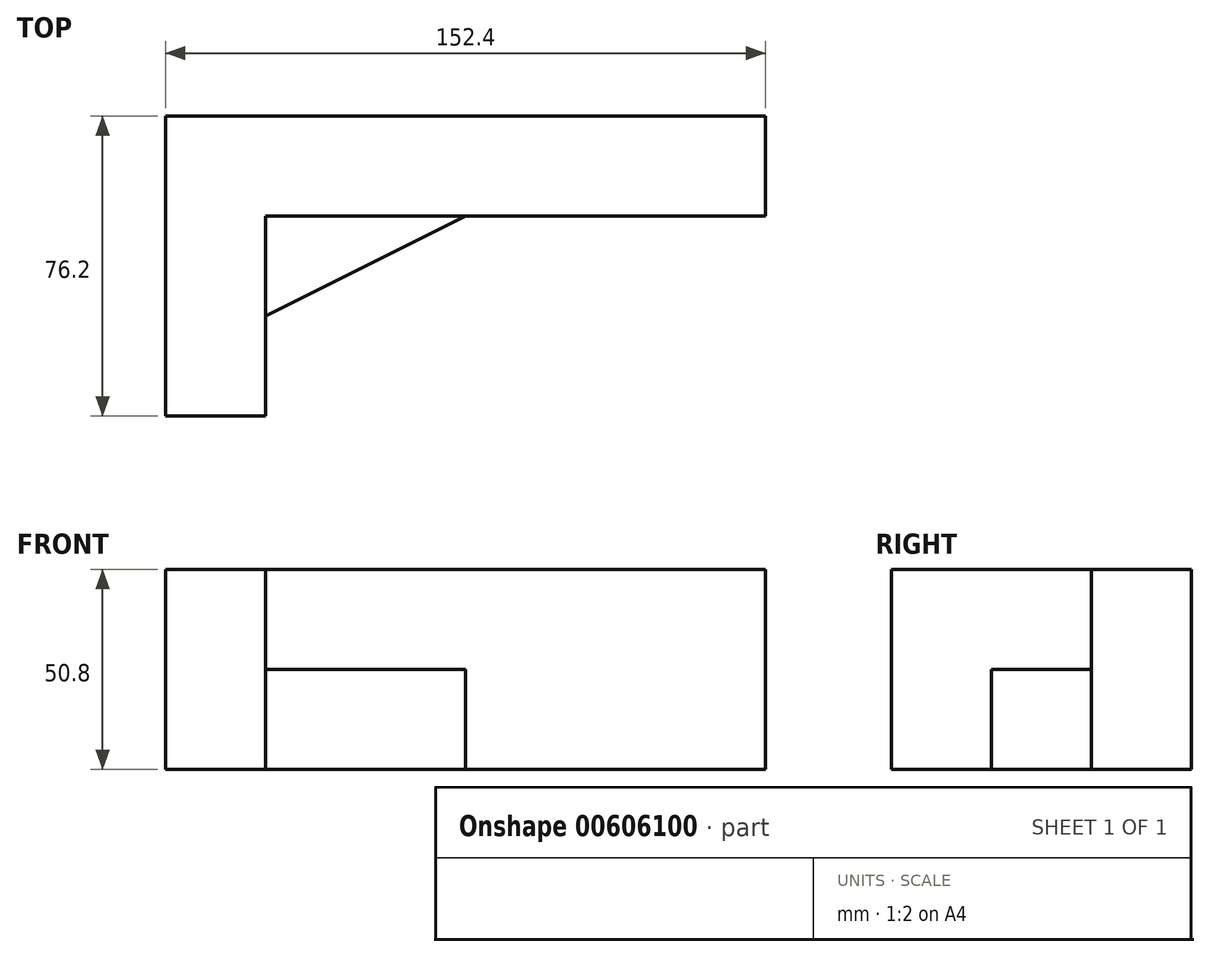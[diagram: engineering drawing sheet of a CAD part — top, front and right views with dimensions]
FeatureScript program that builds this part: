
annotation { "Feature Type Name" : "Feature", "Feature Type Description" : "" }
export const myFeature = defineFeature(function(context is Context, id is Id, definition is map)
    precondition{}
    {
        {
            var Q0;
            Q0=qCreatedBy(makeId("Front.planeOp"),FACE);
            var sketch = newSketch(context, id + "F0", { "sketchPlane" : qUnion([Q0])});
            skLineSegment(sketch, "E0", {"start": v(0, 0) * mm, "end": v(0, 50.8) * mm});
            skLineSegment(sketch, "E1", {"start": v(0, 50.8) * mm, "end": v(152.4, 50.8) * mm});
            skLineSegment(sketch, "E2", {"start": v(152.4, 50.8) * mm, "end": v(152.4, 0) * mm});
            skLineSegment(sketch, "E3", {"start": v(152.4, 0) * mm, "end": v(0, 0) * mm});
            skSolve(sketch);
        }
        {
            var Q0;
            Q0 = qSketchRegion(id + "F0", true);
            extrude(context, id + "F1", {"entities" : qUnion([Q0]), "depth" : 76.2 * mm, "offsetDistance" : 25.4 * mm});
        }
        {
            var Q0;
            Q0=makeQuery(id+"F1.opExtrude","SWEPT_FACE",FACE,{"disambiguationData":[OSD([sQuery(id+"F0.wireOp",EDGE,"E1")])]});
            var sketch = newSketch(context, id + "F2", { "sketchPlane" : qUnion([Q0])});
            skLineSegment(sketch, "E4", {"start": v(25.4, -76.2) * mm, "end": v(25.4, -25.4) * mm});
            skLineSegment(sketch, "E5", {"start": v(25.4, -25.4) * mm, "end": v(152.4, -25.4) * mm});
            skSolve(sketch);
        }
        {
            var Q0;
            Q0 = qSketchRegion(id + "F2", true);
            var Q1;
            {var subQ0=sQuery(id+"F2.wireOp",EDGE,"E4");Q1=makeQuery(id+"F2.imprint","IMPRINT",FACE,{"disambiguationData":[TD([[makeQuery(id+"F2.imprint","IMPRINT",EDGE,{"derivedFrom":subQ0}),-1.0]])]});}
            extrude(context, id + "F3", {"entities" : qUnion([Q0, Q1]), "operationType" : NewBodyOperationType.REMOVE, "oppositeDirection" : true, "depth" : 50.8 * mm, "offsetDistance" : 25.4 * mm});
        }
        {
            var Q0;
            Q0=qCreatedBy(makeId("Top.planeOp"),FACE);
            var sketch = newSketch(context, id + "F4", { "sketchPlane" : qUnion([Q0])});
            skLineSegment(sketch, "E6.0", {"start": v(25.4, -76.2) * mm, "end": v(25.4, -25.4) * mm});
            skLineSegment(sketch, "E7.0", {"start": v(25.4, -25.4) * mm, "end": v(152.4, -25.4) * mm});
            skLineSegment(sketch, "E8.0.2", {"start": v(152.4, -25.4) * mm, "end": v(152.4, 0) * mm});
            skLineSegment(sketch, "E8.0.3", {"start": v(152.4, 0) * mm, "end": v(0, 0) * mm});
            skLineSegment(sketch, "E8.0.4", {"start": v(0, 0) * mm, "end": v(0, -76.2) * mm});
            skLineSegment(sketch, "E8.0.5", {"start": v(0, -76.2) * mm, "end": v(25.4, -76.2) * mm});
            skLineSegment(sketch, "E9", {"start": v(25.4, -50.8) * mm, "end": v(76.2, -25.4) * mm});
            skLineSegment(sketch, "E10", {"start": v(76.2, -25.4) * mm, "end": v(25.4, -25.4) * mm});
            skSolve(sketch);
        }
        {
            var Q0;
            Q0=makeQuery(id+"F4.imprint","IMPRINT",FACE,{"disambiguationData":[TD([[makeQuery(id+"F4.imprint","IMPRINT",EDGE,{"derivedFrom":sQuery(id+"F4.wireOp",EDGE,"E7.0")}),1.0]])]});
            var Q1;
            {var subQ2=sQuery(id+"F4.wireOp",EDGE,"E9");Q1=makeQuery(id+"F4.imprint","IMPRINT",FACE,{"disambiguationData":[TD([[makeQuery(id+"F4.imprint","IMPRINT",EDGE,{"derivedFrom":subQ2}),1.0]])]});}
            extrude(context, id + "F5", {"entities" : qUnion([Q0, Q1]), "operationType" : NewBodyOperationType.ADD, "depth" : 25.4 * mm, "offsetDistance" : 25.4 * mm});
        }
    });
